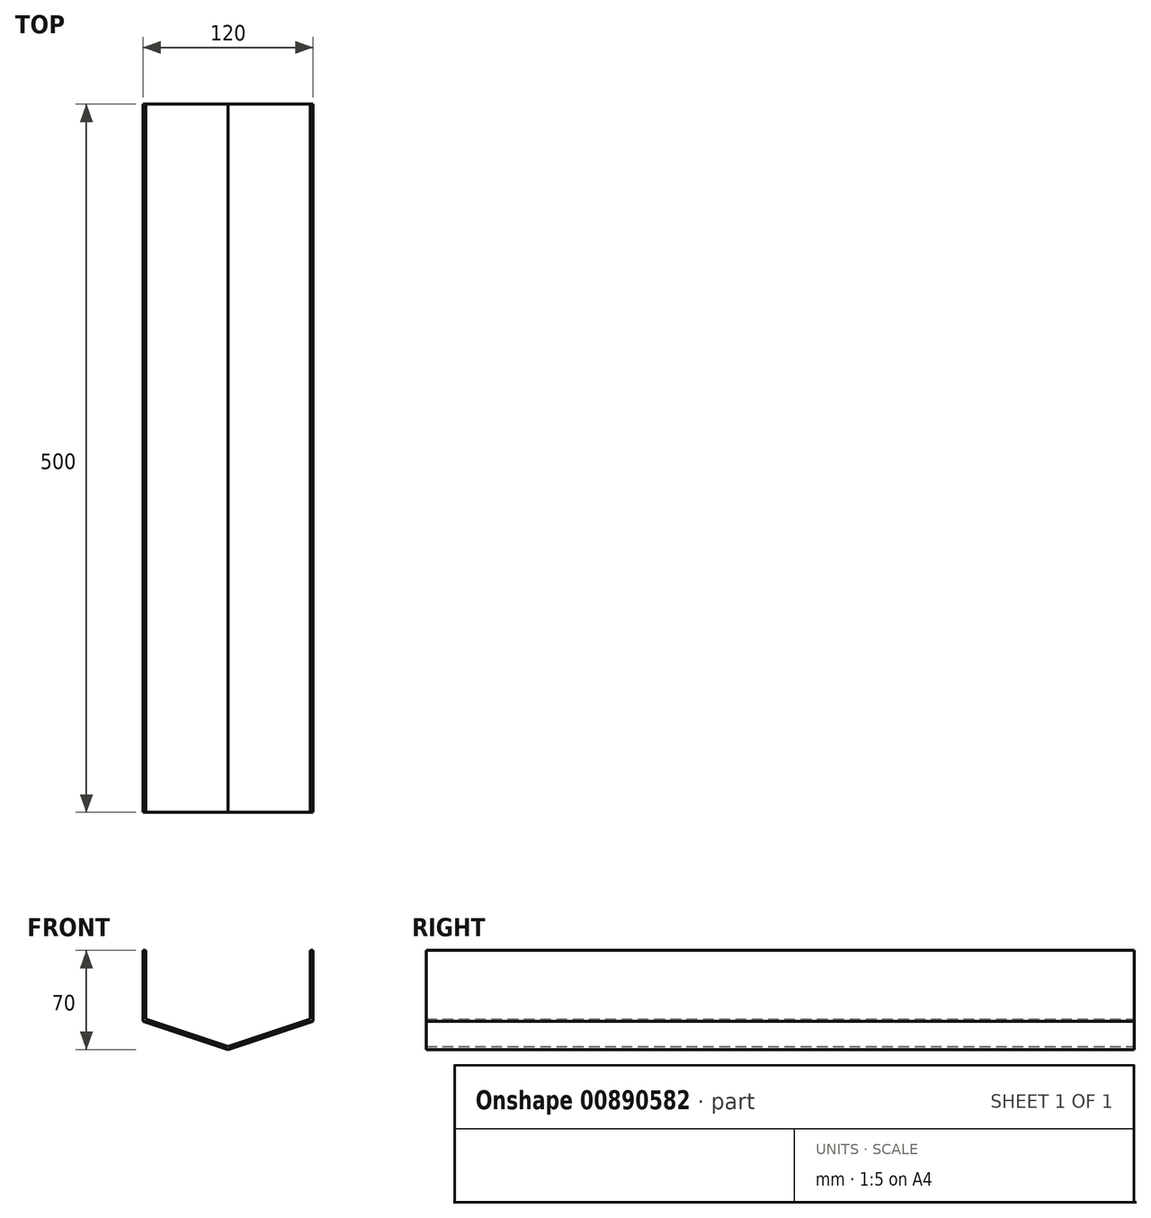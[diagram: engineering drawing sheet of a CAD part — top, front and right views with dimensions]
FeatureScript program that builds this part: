
annotation { "Feature Type Name" : "Feature", "Feature Type Description" : "" }
export const myFeature = defineFeature(function(context is Context, id is Id, definition is map)
    precondition{}
    {
        {
            var Q0;
            Q0=qCreatedBy(makeId("Front.planeOp"),FACE);
            var sketch = newSketch(context, id + "F0", { "sketchPlane" : qUnion([Q0])});
            skLineSegment(sketch, "E0", {"start": v(0, 0) * mm, "end": v(0, 0) * mm});
            skPoint(sketch, "E1.start.orphan", {"position": v(0, 60.4) * mm});
            skLineSegment(sketch, "E2.top", {"start": v(-60, 70) * mm, "end": v(60, 70) * mm});
            skLineSegment(sketch, "E2.left", {"start": v(-60, 20) * mm, "end": v(-60, 70) * mm});
            skLineSegment(sketch, "E2.right", {"start": v(60, 20) * mm, "end": v(60, 70) * mm});
            skLineSegment(sketch, "E3", {"start": v(-60, 20) * mm, "end": v(0, 0) * mm});
            skLineSegment(sketch, "E4", {"start": v(0, 0) * mm, "end": v(60, 20) * mm});
            skPoint(sketch, "E5.orphan", {"position": v(-60, 30) * mm});
            skPoint(sketch, "E6.orphan", {"position": v(60, -30) * mm});
            skSolve(sketch);
        }
        {
            var Q0;
            Q0=makeQuery(id+"F0.imprint","IMPRINT",FACE,{"disambiguationData":[TD([[makeQuery(id+"F0.imprint","IMPRINT",EDGE,{"derivedFrom":sQuery(id+"F0.wireOp",EDGE,"E2.top")}),-1.0]])]});
            extrude(context, id + "F1", {"entities" : qUnion([Q0]), "depth" : 500 * mm, "offsetDistance" : 25 * mm});
        }
        {
            var Q0;
            Q0=makeQuery(id+"F1.opExtrude","SWEPT_FACE",FACE,{"disambiguationData":[OSD([sQuery(id+"F0.wireOp",EDGE,"E2.top")])]});
            var Q1;
            Q1=makeQuery(id+"F1.opExtrude","CAP_FACE",FACE,{"disambiguationData":[OSD([sQuery(id+"F0.wireOp",EDGE,"E2.top"),sQuery(id+"F0.wireOp",EDGE,"E2.left"),sQuery(id+"F0.wireOp",EDGE,"E2.right"),sQuery(id+"F0.wireOp",EDGE,"E3"),sQuery(id+"F0.wireOp",EDGE,"E4")])],"isStart":false});
            var Q2;
            Q2=makeQuery(id+"F1.opExtrude","CAP_FACE",FACE,{"disambiguationData":[OSD([sQuery(id+"F0.wireOp",EDGE,"E2.top"),sQuery(id+"F0.wireOp",EDGE,"E2.left"),sQuery(id+"F0.wireOp",EDGE,"E2.right"),sQuery(id+"F0.wireOp",EDGE,"E3"),sQuery(id+"F0.wireOp",EDGE,"E4")])],"isStart":true});
            shell(context, id + "F2", {"entities" : qUnion([Q0, Q1, Q2]), "thickness" : 2 * mm});
        }
    });
